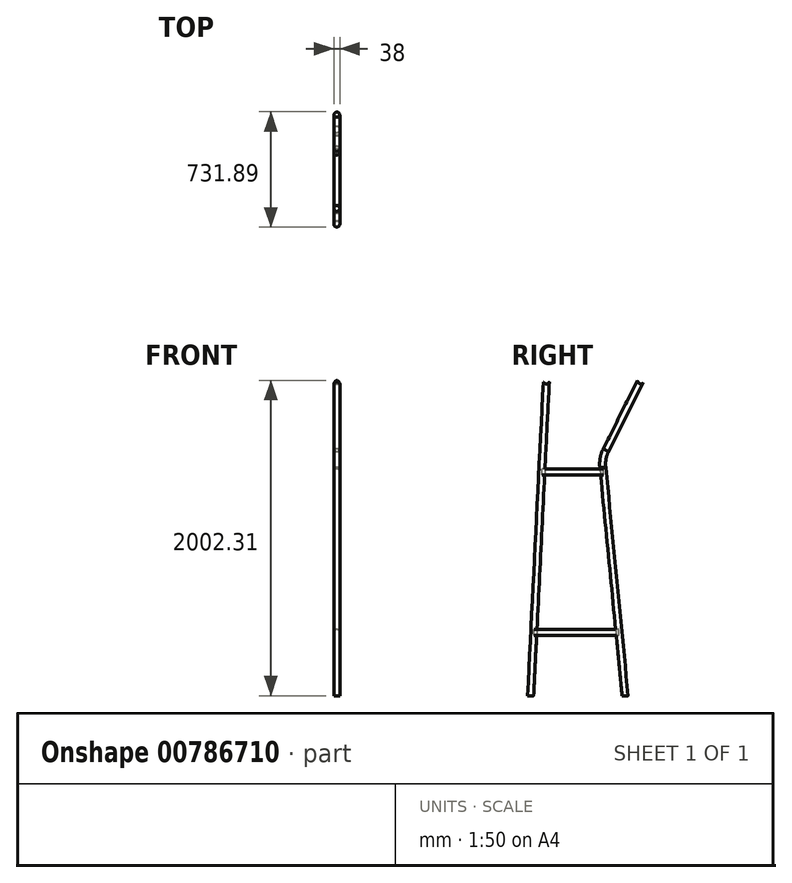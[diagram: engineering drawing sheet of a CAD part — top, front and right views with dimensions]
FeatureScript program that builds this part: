
annotation { "Feature Type Name" : "Feature", "Feature Type Description" : "" }
export const myFeature = defineFeature(function(context is Context, id is Id, definition is map)
    precondition{}
    {
        {
            var Q0;
            Q0=qCreatedBy(makeId("Right.planeOp"),FACE);
            var sketch = newSketch(context, id + "F0", { "sketchPlane" : qUnion([Q0])});
            skLineSegment(sketch, "E0", {"start": v(-71.5, 2001.97) * mm, "end": v(-71.5, 1.97) * mm, "construction": true});
            skLineSegment(sketch, "E1", {"start": v(-71.5, 1.97) * mm, "end": v(528.5, 1.97) * mm, "construction": true});
            skLineSegment(sketch, "E2", {"start": v(-71.5, 2001.97) * mm, "end": v(28.5, 2001.97) * mm, "construction": true});
            skLineSegment(sketch, "E3", {"start": v(28.5, 2001.97) * mm, "end": v(628.5, 2001.97) * mm, "construction": true});
            skSolve(sketch);
        }
        {
            var Q0;
            Q0=qCreatedBy(makeId("Right.planeOp"),FACE);
            var sketch = newSketch(context, id + "F1", { "sketchPlane" : qUnion([Q0])});
            skLineSegment(sketch, "E4", {"start": v(-71.5, 1.97) * mm, "end": v(28.5, 2001.97) * mm});
            skSolve(sketch);
        }
        {
            var Q0;
            Q0=qCreatedBy(makeId("Right.planeOp"),FACE);
            var sketch = newSketch(context, id + "F2", { "sketchPlane" : qUnion([Q0])});
            skLineSegment(sketch, "E5", {"start": v(528.5, 1.97) * mm, "end": v(386.8, 1452.41) * mm});
            skLineSegment(sketch, "E6", {"start": v(407.16, 1561.69) * mm, "end": v(628.5, 2001.97) * mm});
            skPoint(sketch, "E7.visualSharp", {"position": v(381.17, 1510) * mm});
            skArc(sketch, "E7.filletArc", {"start": v(407.16, 1561.69) * mm, "mid": v(389.23, 1508.5) * mm, "end": v(386.8, 1452.41) * mm});
            skSolve(sketch);
        }
        {
            var Q0;
            Q0=qCreatedBy(makeId("Right.planeOp"),FACE);
            var sketch = newSketch(context, id + "F3", { "sketchPlane" : qUnion([Q0])});
            skLineSegment(sketch, "E8", {"start": v(-51.5, 401.97) * mm, "end": v(489.42, 401.97) * mm});
            skSolve(sketch);
        }
        {
            var Q0;
            Q0=qCreatedBy(makeId("Right.planeOp"),FACE);
            var sketch = newSketch(context, id + "F4", { "sketchPlane" : qUnion([Q0])});
            skLineSegment(sketch, "E9", {"start": v(-0.5, 1421.97) * mm, "end": v(389.77, 1421.97) * mm});
            skSolve(sketch);
        }
        {
            var Q0;
            Q0=qCreatedBy(makeId("Top.planeOp"),FACE);
            var sketch = newSketch(context, id + "F5", { "sketchPlane" : qUnion([Q0])});
            skCircle(sketch, "E10", {"center": v(0, -71.6) * mm, "radius": 19 * mm});
            skSolve(sketch);
        }
        {
            var Q0;
            Q0=qCreatedBy(makeId("Top.planeOp"),FACE);
            var sketch = newSketch(context, id + "F6", { "sketchPlane" : qUnion([Q0])});
            skCircle(sketch, "E11", {"center": v(0, 528.69) * mm, "radius": 19 * mm});
            skSolve(sketch);
        }
        {
            var Q0;
            Q0=qCreatedBy(makeId("Front.planeOp"),FACE);
            var sketch = newSketch(context, id + "F7", { "sketchPlane" : qUnion([Q0])});
            skCircle(sketch, "E12", {"center": v(0, 1421.97) * mm, "radius": 19 * mm});
            skSolve(sketch);
        }
        {
            var Q0;
            Q0=qCreatedBy(makeId("Front.planeOp"),FACE);
            var sketch = newSketch(context, id + "F8", { "sketchPlane" : qUnion([Q0])});
            skCircle(sketch, "E13", {"center": v(0, 401.97) * mm, "radius": 19 * mm});
            skSolve(sketch);
        }
        {
            var Q0;
            Q0=makeQuery(id+"F6.imprint","IMPRINT",FACE,{"disambiguationData":[TD([[makeQuery(id+"F6.imprint","IMPRINT",EDGE,{"derivedFrom":sQuery(id+"F6.wireOp",EDGE,"E11")}),1.0]])]});
            var Q1;
            Q1 = qConstructionFilter(qBodyType(qCreatedBy(id + "F2" ,EDGE), BodyType.WIRE), ConstructionObject.NO);
            sweep(context, id + "F9", {"profiles" : qUnion([Q0]), "path" : qUnion([Q1])});
        }
        {
            var Q0;
            Q0=makeQuery(id+"F5.imprint","IMPRINT",FACE,{"disambiguationData":[TD([[makeQuery(id+"F5.imprint","IMPRINT",EDGE,{"derivedFrom":sQuery(id+"F5.wireOp",EDGE,"E10")}),1.0]])]});
            var Q1;
            Q1=sQuery(id+"F1.wireOp",EDGE,"E4");
            sweep(context, id + "F10", {"profiles" : qUnion([Q0]), "path" : qUnion([Q1])});
        }
        {
            var Q0;
            Q0=makeQuery(id+"F8.imprint","IMPRINT",FACE,{"disambiguationData":[TD([[makeQuery(id+"F8.imprint","IMPRINT",EDGE,{"derivedFrom":sQuery(id+"F8.wireOp",EDGE,"E13")}),1.0]])]});
            var Q1;
            Q1=sQuery(id+"F3.wireOp",EDGE,"E8");
            sweep(context, id + "F11", {"profiles" : qUnion([Q0]), "path" : qUnion([Q1])});
        }
        {
            var Q0;
            Q0 = qSketchRegion(id + "F7", true);
            var Q1;
            Q1 = qConstructionFilter(qBodyType(qCreatedBy(id + "F4" ,EDGE), BodyType.WIRE), ConstructionObject.NO);
            sweep(context, id + "F12", {"profiles" : qUnion([Q0]), "path" : qUnion([Q1])});
        }
        {
            var Q0;
            Q0=qCreatedBy(makeId("Right.planeOp"),FACE);
            var sketch = newSketch(context, id + "F13", { "sketchPlane" : qUnion([Q0])});
            skCircle(sketch, "E14", {"center": v(28.5, 2001.97) * mm, "radius": 21 * mm});
            skCircle(sketch, "E15", {"center": v(628.5, 2001.97) * mm, "radius": 21 * mm});
            skSolve(sketch);
        }
        {
            var Q0;
            Q0 = qSketchRegion(id + "F13", true);
            extrude(context, id + "F14", {"entities" : qUnion([Q0]), "operationType" : NewBodyOperationType.REMOVE, "oppositeDirection" : true, "depth" : 100 * mm, "offsetDistance" : 25 * mm, "hasSecondDirection" : true, "secondDirectionOppositeDirection" : false, "secondDirectionDepth" : 25 * mm});
        }
    });
